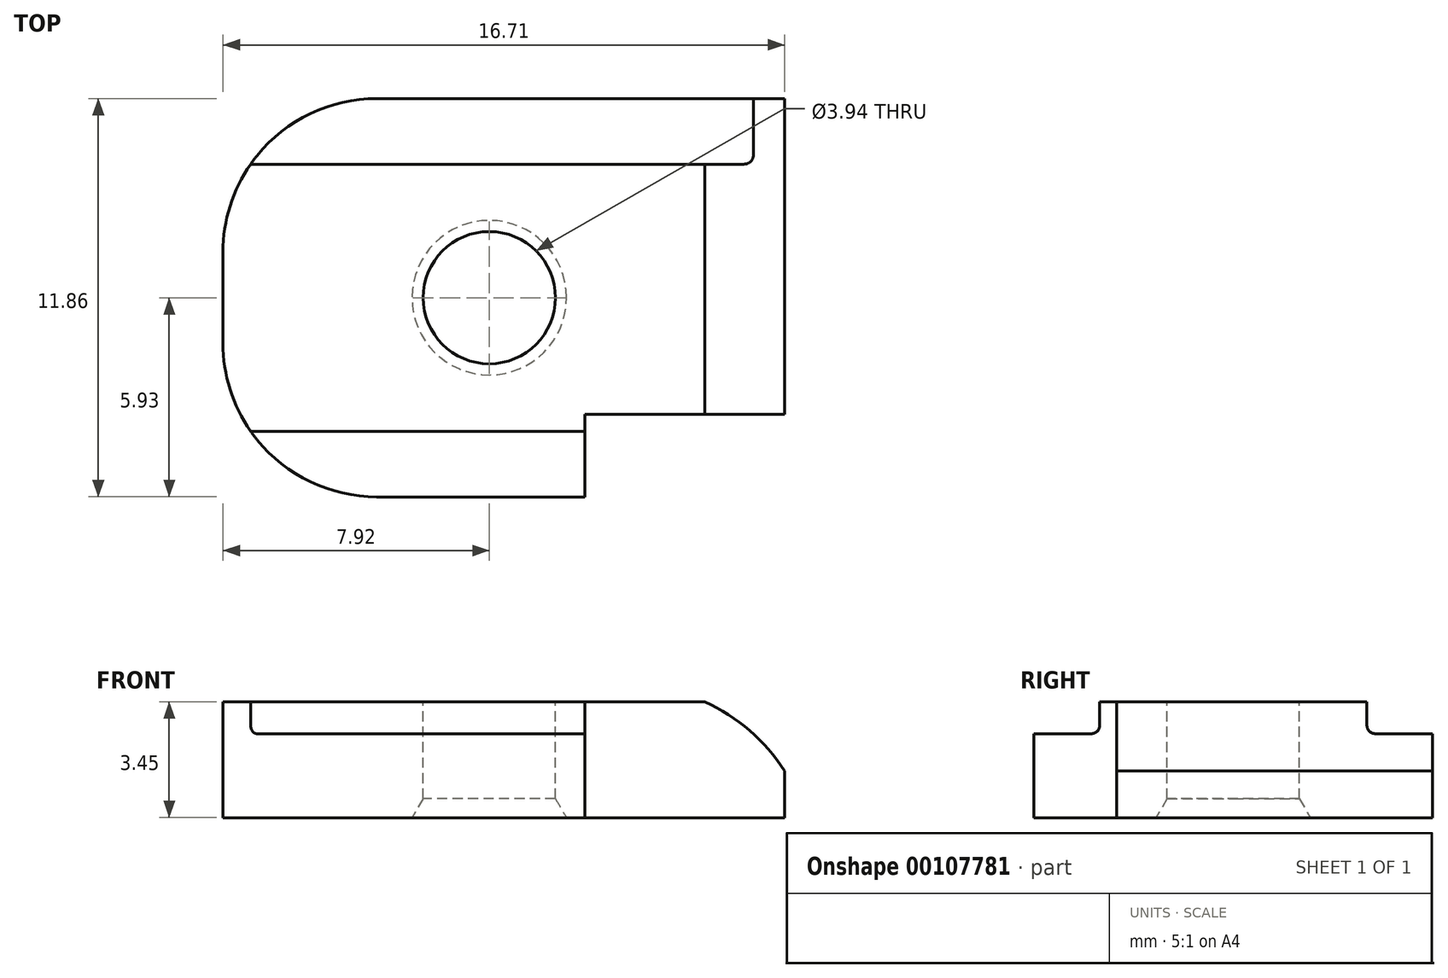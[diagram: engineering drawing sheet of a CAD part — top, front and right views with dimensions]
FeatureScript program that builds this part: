
annotation { "Feature Type Name" : "Feature", "Feature Type Description" : "" }
export const myFeature = defineFeature(function(context is Context, id is Id, definition is map)
    precondition{}
    {
        {
            var Q0;
            Q0=qCreatedBy(makeId("Top.planeOp"),FACE);
            var sketch = newSketch(context, id + "F0", { "sketchPlane" : qUnion([Q0])});
            skLineSegment(sketch, "E0.bottom", {"start": v(-7.92, -5.93) * mm, "end": v(2.84, -5.93) * mm});
            skLineSegment(sketch, "E0.top", {"start": v(-7.92, 5.93) * mm, "end": v(8.79, 5.93) * mm});
            skLineSegment(sketch, "E0.left", {"start": v(-7.92, -5.93) * mm, "end": v(-7.92, 5.93) * mm});
            skLineSegment(sketch, "E0.right", {"start": v(8.79, -3.47) * mm, "end": v(8.79, 5.93) * mm});
            skCircle(sketch, "E1", {"center": v(0, 0) * mm, "radius": 1.97 * mm});
            skLineSegment(sketch, "E2", {"start": v(2.84, -5.93) * mm, "end": v(2.84, -3.47) * mm});
            skLineSegment(sketch, "E3", {"start": v(2.84, -3.47) * mm, "end": v(8.79, -3.47) * mm});
            skSolve(sketch);
        }
        {
            var Q0;
            Q0=makeQuery(id+"F0.imprint","IMPRINT",FACE,{"disambiguationData":[TD([[makeQuery(id+"F0.imprint","IMPRINT",EDGE,{"derivedFrom":sQuery(id+"F0.wireOp",EDGE,"E0.bottom")}),1.0]])]});
            extrude(context, id + "F1", {"entities" : qUnion([Q0]), "oppositeDirection" : true, "depth" : 3.45 * mm});
        }
        {
            var Q0;
            Q0=makeQuery(id+"F1.opExtrude","SWEPT_FACE",FACE,{"disambiguationData":[OSD([sQuery(id+"F0.wireOp",EDGE,"E0.left")])]});
            var sketch = newSketch(context, id + "F2", { "sketchPlane" : qUnion([Q0])});
            skLineSegment(sketch, "E4", {"start": v(-5.93, -0.95) * mm, "end": v(-3.98, -0.95) * mm});
            skLineSegment(sketch, "E5", {"start": v(-3.98, -0.95) * mm, "end": v(-3.98, 0) * mm});
            skLineSegment(sketch, "E6", {"start": v(3.98, 0) * mm, "end": v(3.98, -0.95) * mm});
            skLineSegment(sketch, "E7", {"start": v(3.98, -0.95) * mm, "end": v(5.93, -0.95) * mm});
            skLineSegment(sketch, "E8", {"start": v(-5.93, -0.95) * mm, "end": v(-5.93, 0) * mm});
            skLineSegment(sketch, "E9", {"start": v(-5.93, 0) * mm, "end": v(-3.98, 0) * mm});
            skLineSegment(sketch, "E10", {"start": v(3.98, 0) * mm, "end": v(5.93, 0) * mm});
            skLineSegment(sketch, "E11", {"start": v(5.93, 0) * mm, "end": v(5.93, -0.95) * mm});
            skSolve(sketch);
        }
        {
            var Q0;
            Q0 = qSketchRegion(id + "F2", true);
            extrude(context, id + "F3", {"entities" : qUnion([Q0]), "operationType" : NewBodyOperationType.REMOVE, "endBound" : BoundingType.THROUGH_ALL, "oppositeDirection" : true, "depth" : 25.4 * mm});
        }
        {
            var Q0;
            Q0=makeQuery(id+"F1.opExtrude","SWEPT_EDGE",EDGE,{"disambiguationData":[OSD([sQuery(id+"F0.wireOp",EDGE,"E0.bottom"),sQuery(id+"F0.wireOp",EDGE,"E0.left")])]});
            var Q1;
            Q1=makeQuery(id+"F1.opExtrude","SWEPT_EDGE",EDGE,{"disambiguationData":[OSD([sQuery(id+"F0.wireOp",EDGE,"E0.top"),sQuery(id+"F0.wireOp",EDGE,"E0.left")])]});
            fillet(context, id + "F4", {"entities" : qUnion([Q0, Q1]), "radius" : 4.57 * mm, "tangentPropagation" : true, "allowEdgeOverflow" : false});
        }
        {
            var Q0;
            Q0=makeQuery(id+"F1.opExtrude","SWEPT_FACE",FACE,{"disambiguationData":[OSD([sQuery(id+"F0.wireOp",EDGE,"E3")])]});
            var sketch = newSketch(context, id + "F5", { "sketchPlane" : qUnion([Q0])});
            skArc(sketch, "E12", {"start": v(8.79, -2.06) * mm, "mid": v(7.75, -0.86) * mm, "end": v(6.42, 0) * mm});
            skLineSegment(sketch, "E13", {"start": v(6.42, 0) * mm, "end": v(8.79, 0) * mm});
            skLineSegment(sketch, "E14", {"start": v(8.79, 0) * mm, "end": v(8.79, -2.06) * mm});
            skSolve(sketch);
        }
        {
            var Q0;
            Q0 = qSketchRegion(id + "F5", true);
            extrude(context, id + "F6", {"entities" : qUnion([Q0]), "operationType" : NewBodyOperationType.REMOVE, "endBound" : BoundingType.THROUGH_ALL, "oppositeDirection" : true, "depth" : 25.4 * mm});
        }
        {
            var Q0;
            Q0=makeQuery(id+"F3.boolean.opBoolean","COPY",EDGE,{"derivedFrom":makeQuery(id+"F3.opExtrude","SWEPT_EDGE",EDGE,{"disambiguationData":[OSD([sQuery(id+"F0.wireOp",EDGE,"E0.left"),sQuery(id+"F2.wireOp",EDGE,"E6"),sQuery(id+"F2.wireOp",EDGE,"E10")])]})});
            var Q1;
            Q1=makeQuery(id+"F3.boolean.opBoolean","COPY",EDGE,{"derivedFrom":makeQuery(id+"F3.opExtrude","SWEPT_EDGE",EDGE,{"disambiguationData":[OSD([sQuery(id+"F0.wireOp",EDGE,"E0.left"),sQuery(id+"F2.wireOp",EDGE,"E5"),sQuery(id+"F2.wireOp",EDGE,"E9")])]})});
            var Q2;
            Q2=makeQuery(id+"F3.boolean.opBoolean","COPY",EDGE,{"derivedFrom":makeQuery(id+"F3.opExtrude","SWEPT_EDGE",EDGE,{"disambiguationData":[OSD([sQuery(id+"F2.wireOp",EDGE,"E6"),sQuery(id+"F2.wireOp",EDGE,"E7")])]})});
            var Q3;
            Q3=makeQuery(id+"F3.boolean.opBoolean","COPY",EDGE,{"derivedFrom":makeQuery(id+"F3.opExtrude","SWEPT_EDGE",EDGE,{"disambiguationData":[OSD([sQuery(id+"F2.wireOp",EDGE,"E4"),sQuery(id+"F2.wireOp",EDGE,"E5")])]})});
            fillet(context, id + "F7", {"entities" : qUnion([Q0, Q1, Q2, Q3]), "radius" : 0.25 * mm, "tangentPropagation" : true, "allowEdgeOverflow" : false});
        }
        {
            var Q0;
            Q0=makeQuery(id+"F1.opExtrude","CAP_EDGE",EDGE,{"disambiguationData":[OSD([sQuery(id+"F0.wireOp",EDGE,"E1")])],"isStart":false});
            chamfer(context, id + "F8", {"entities" : qUnion([Q0]), "chamferType" : ChamferType.OFFSET_ANGLE, "width" : 0.33 * mm, "oppositeDirection" : false, "angle" : 60 * degree, "tangentPropagation" : true});
        }
    });
